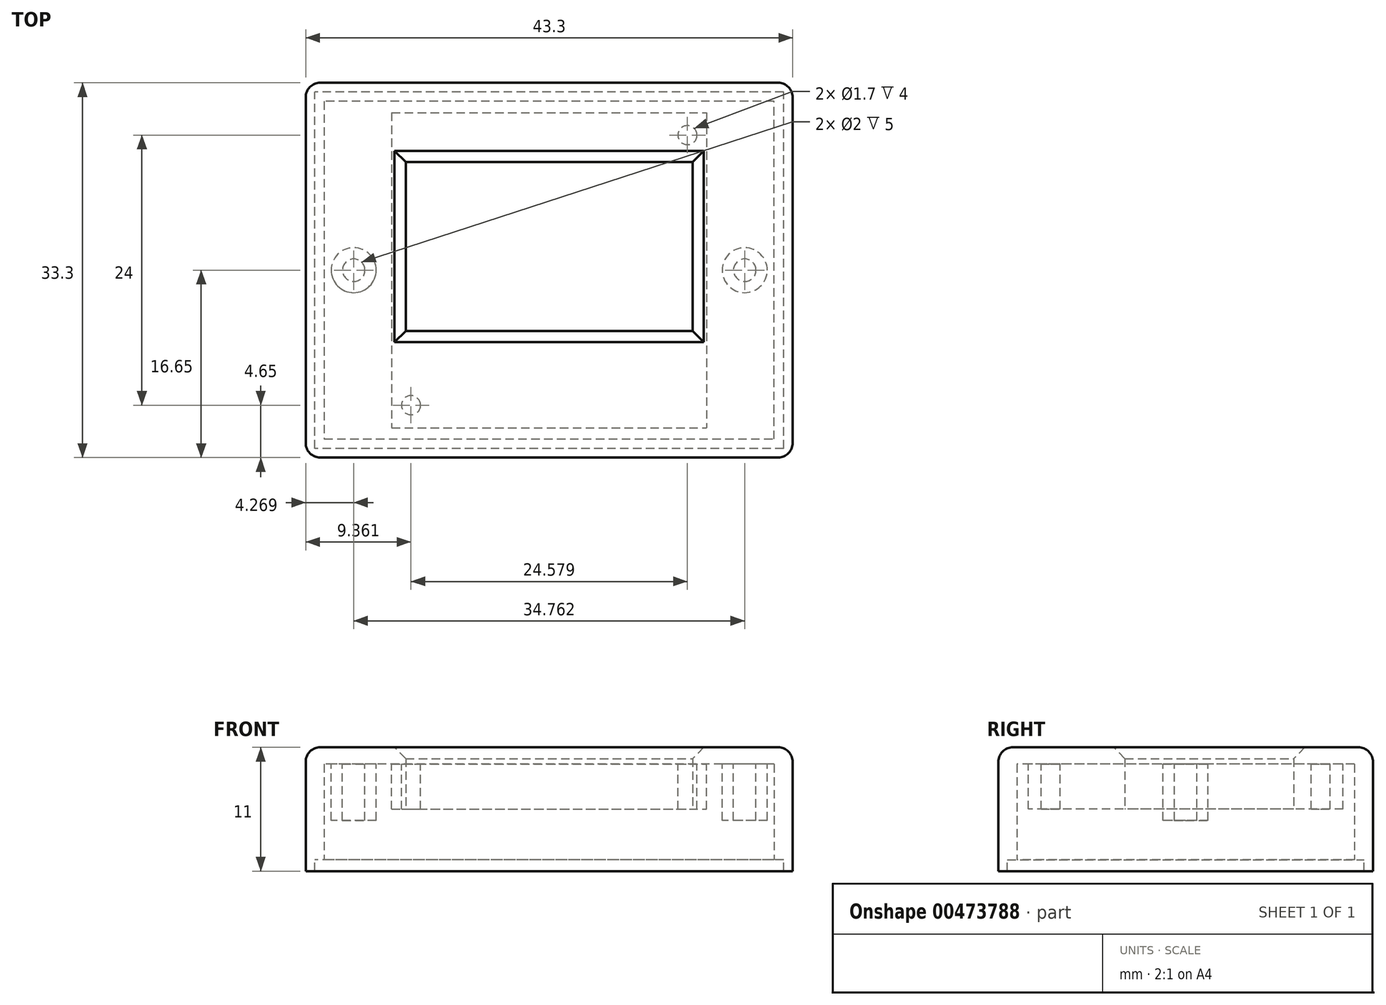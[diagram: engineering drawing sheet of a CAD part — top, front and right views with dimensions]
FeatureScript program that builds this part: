
annotation { "Feature Type Name" : "Feature", "Feature Type Description" : "" }
export const myFeature = defineFeature(function(context is Context, id is Id, definition is map)
    precondition{}
    {
        {
            var Q0;
            Q0=qCreatedBy(makeId("Top.planeOp"),FACE);
            var sketch = newSketch(context, id + "F0", { "sketchPlane" : qUnion([Q0])});
            skPoint(sketch, "E0.middle", {"position": v(0, 0) * mm});
            skLineSegment(sketch, "E1.0", {"start": v(21.65, -16.65) * mm, "end": v(-21.65, -16.65) * mm});
            skLineSegment(sketch, "E1.1", {"start": v(21.65, -16.65) * mm, "end": v(21.65, 16.65) * mm});
            skLineSegment(sketch, "E1.2", {"start": v(21.65, 16.65) * mm, "end": v(-21.65, 16.65) * mm});
            skLineSegment(sketch, "E1.3", {"start": v(-21.65, -16.65) * mm, "end": v(-21.65, 16.65) * mm});
            skSolve(sketch);
        }
        {
            var Q0;
            Q0=qSketchRegion(id+"F0",true);
            extrude(context, id + "F1", {"entities" : qUnion([Q0]), "depth" : 10 * mm});
        }
        {
            var Q0;
            Q0=makeQuery(id+"F0.imprint","IMPRINT",FACE,{"disambiguationData":[TD([[makeQuery(id+"F0.imprint","IMPRINT",EDGE,{"derivedFrom":sQuery(id+"F0.wireOp",EDGE,"E1.0")}),-1.0]])]});
            var sketch = newSketch(context, id + "F2", { "sketchPlane" : qUnion([Q0])});
            skLineSegment(sketch, "E2.0", {"start": v(-20, 15) * mm, "end": v(-20, -15) * mm});
            skLineSegment(sketch, "E2.1", {"start": v(20, 15) * mm, "end": v(-20, 15) * mm});
            skLineSegment(sketch, "E2.2", {"start": v(20, -15) * mm, "end": v(20, 15) * mm});
            skLineSegment(sketch, "E2.3", {"start": v(-20, -15) * mm, "end": v(20, -15) * mm});
            skSolve(sketch);
        }
        {
            var Q0;
            Q0=qSketchRegion(id+"F2",true);
            extrude(context, id + "F3", {"entities" : qUnion([Q0]), "operationType" : NewBodyOperationType.REMOVE, "depth" : 8.5 * mm});
        }
        {
            var Q0;
            Q0=makeQuery(id+"F3.boolean.opBoolean","COPY",FACE,{"derivedFrom":makeQuery(id+"F3.opExtrude","CAP_FACE",FACE,{"disambiguationData":[OSD([sQuery(id+"F2.wireOp",EDGE,"E2.0"),sQuery(id+"F2.wireOp",EDGE,"E2.1"),sQuery(id+"F2.wireOp",EDGE,"E2.2"),sQuery(id+"F2.wireOp",EDGE,"E2.3")])],"isStart":false})});
            var sketch = newSketch(context, id + "F4", { "sketchPlane" : qUnion([Q0])});
            skLineSegment(sketch, "E3.bottom", {"start": v(-21.65, 16.65) * mm, "end": v(21.65, 16.65) * mm});
            skLineSegment(sketch, "E3.top", {"start": v(-21.65, -16.65) * mm, "end": v(21.65, -16.65) * mm});
            skLineSegment(sketch, "E3.left", {"start": v(-21.65, 16.65) * mm, "end": v(-21.65, -16.65) * mm});
            skLineSegment(sketch, "E3.right", {"start": v(21.65, 16.65) * mm, "end": v(21.65, -16.65) * mm});
            skLineSegment(sketch, "E4.bottom", {"start": v(-14, -14) * mm, "end": v(14, -14) * mm});
            skLineSegment(sketch, "E4.top", {"start": v(-14, 14) * mm, "end": v(14, 14) * mm});
            skLineSegment(sketch, "E4.left", {"start": v(-14, -14) * mm, "end": v(-14, 14) * mm});
            skLineSegment(sketch, "E4.right", {"start": v(14, -14) * mm, "end": v(14, 14) * mm});
            skPoint(sketch, "E4.middle", {"position": v(0, 0) * mm});
            skLineSegment(sketch, "E5.bottom", {"start": v(-12.75, -9.6) * mm, "end": v(12.75, -9.6) * mm});
            skLineSegment(sketch, "E5.top", {"start": v(-12.75, 5.4) * mm, "end": v(12.75, 5.4) * mm});
            skLineSegment(sketch, "E5.left", {"start": v(-12.75, -9.6) * mm, "end": v(-12.75, 5.4) * mm});
            skLineSegment(sketch, "E5.right", {"start": v(12.75, -9.6) * mm, "end": v(12.75, 5.4) * mm});
            skPoint(sketch, "E6", {"position": v(0, -9.6) * mm});
            skLineSegment(sketch, "E7", {"start": v(0, -15) * mm, "end": v(0, 15) * mm, "construction": true});
            skCircle(sketch, "E8", {"center": v(-12.29, -12) * mm, "radius": 0.85 * mm});
            skLineSegment(sketch, "E9", {"start": v(-21.65, 0) * mm, "end": v(21.65, 0) * mm, "construction": true});
            skCircle(sketch, "E10.MirrorC", {"center": v(-12.29, 12) * mm, "radius": 0.85 * mm});
            skLineSegment(sketch, "E11.MirrorCS", {"start": v(0, 15) * mm, "end": v(0, -15) * mm, "construction": true});
            skCircle(sketch, "E12.MirrorC", {"center": v(12.29, 12) * mm, "radius": 0.85 * mm});
            skCircle(sketch, "E13.MirrorC", {"center": v(12.29, -12) * mm, "radius": 0.85 * mm});
            skSolve(sketch);
        }
        {
            var Q0;
            Q0=makeQuery(id+"F4.imprint","IMPRINT",FACE,{"disambiguationData":[TD([[makeQuery(id+"F4.imprint","IMPRINT",EDGE,{"derivedFrom":sQuery(id+"F4.wireOp",EDGE,"E5.bottom")}),1.0]])]});
            extrude(context, id + "F5", {"entities" : qUnion([Q0]), "operationType" : NewBodyOperationType.REMOVE, "oppositeDirection" : true, "depth" : 25 * mm});
        }
        {
            var Q0;
            Q0=makeQuery(id+"F4.imprint","IMPRINT",FACE,{"disambiguationData":[TD([[makeQuery(id+"F4.imprint","IMPRINT",EDGE,{"derivedFrom":sQuery(id+"F4.wireOp",EDGE,"E12.MirrorC")}),1.0]])]});
            var Q1;
            Q1=makeQuery(id+"F4.imprint","IMPRINT",FACE,{"disambiguationData":[TD([[makeQuery(id+"F4.imprint","IMPRINT",EDGE,{"derivedFrom":sQuery(id+"F4.wireOp",EDGE,"E10.MirrorC")}),-1.0]])]});
            var Q2;
            Q2=makeQuery(id+"F4.imprint","IMPRINT",FACE,{"disambiguationData":[TD([[makeQuery(id+"F4.imprint","IMPRINT",EDGE,{"derivedFrom":sQuery(id+"F4.wireOp",EDGE,"E8")}),1.0]])]});
            var Q3;
            Q3=makeQuery(id+"F4.imprint","IMPRINT",FACE,{"disambiguationData":[TD([[makeQuery(id+"F4.imprint","IMPRINT",EDGE,{"derivedFrom":sQuery(id+"F4.wireOp",EDGE,"E13.MirrorC")}),-1.0]])]});
            extrude(context, id + "F6", {"entities" : qUnion([Q0, Q1, Q2, Q3]), "operationType" : NewBodyOperationType.ADD, "depth" : 4 * mm});
        }
        {
            var Q0;
            Q0=makeQuery(id+"F1.opExtrude","CAP_FACE",FACE,{"disambiguationData":[OSD([sQuery(id+"F0.wireOp",EDGE,"E1.0"),sQuery(id+"F0.wireOp",EDGE,"E1.1"),sQuery(id+"F0.wireOp",EDGE,"E1.2"),sQuery(id+"F0.wireOp",EDGE,"E1.3")])],"isStart":true});
            var sketch = newSketch(context, id + "F7", { "sketchPlane" : qUnion([Q0])});
            skLineSegment(sketch, "E14.0", {"start": v(20.85, 15.85) * mm, "end": v(-20.85, 15.85) * mm});
            skLineSegment(sketch, "E14.1", {"start": v(20.85, 15.85) * mm, "end": v(20.85, -15.85) * mm});
            skLineSegment(sketch, "E14.2", {"start": v(20.85, -15.85) * mm, "end": v(-20.85, -15.85) * mm});
            skLineSegment(sketch, "E14.3", {"start": v(-20.85, 15.85) * mm, "end": v(-20.85, -15.85) * mm});
            skLineSegment(sketch, "E15.bottom", {"start": v(-21.65, 16.65) * mm, "end": v(21.65, 16.65) * mm});
            skLineSegment(sketch, "E15.top", {"start": v(-21.65, -16.65) * mm, "end": v(21.65, -16.65) * mm});
            skLineSegment(sketch, "E15.left", {"start": v(-21.65, 16.65) * mm, "end": v(-21.65, -16.65) * mm});
            skLineSegment(sketch, "E15.right", {"start": v(21.65, 16.65) * mm, "end": v(21.65, -16.65) * mm});
            skSolve(sketch);
        }
        {
            var Q0;
            Q0=qSketchRegion(id+"F7",true);
            extrude(context, id + "F8", {"entities" : qUnion([Q0]), "operationType" : NewBodyOperationType.ADD, "depth" : 1 * mm});
        }
        {
            var Q0;
            Q0=makeQuery(id+"F4.imprint","IMPRINT",FACE,{"disambiguationData":[TD([[makeQuery(id+"F4.imprint","IMPRINT",EDGE,{"derivedFrom":sQuery(id+"F4.wireOp",EDGE,"E4.bottom")}),-1.0]])]});
            var sketch = newSketch(context, id + "F9", { "sketchPlane" : qUnion([Q0])});
            skCircle(sketch, "E16", {"center": v(-17.38, 0) * mm, "radius": 2 * mm});
            skCircle(sketch, "E17", {"center": v(-17.38, 0) * mm, "radius": 1 * mm});
            skSolve(sketch);
        }
        {
            var Q0;
            Q0=qSketchRegion(id+"F9",true);
            extrude(context, id + "F10", {"entities" : qUnion([Q0]), "depth" : 5 * mm});
        }
        {
            var Q0;
            Q0=makeQuery(id+"F10.opExtrude","SWEPT_BODY",BODY,{"disambiguationData":[OSD([sQuery(id+"F9.wireOp",EDGE,"E16"),sQuery(id+"F9.wireOp",EDGE,"E17")])]});
            var Q1;
            Q1=qCreatedBy(makeId("Right.planeOp"),FACE);
            mirror(context, id + "F11", {"operationType" : NewBodyOperationType.ADD, "entities" : qUnion([Q0]), "mirrorPlane" : qUnion([Q1])});
        }
        {
            var Q0;
            Q0=makeQuery(id+"F5.boolean.opBoolean","INTERSECT",EDGE,{"derivedFrom":[makeQuery(id+"F1.opExtrude","CAP_FACE",FACE,{"disambiguationData":[OSD([sQuery(id+"F0.wireOp",EDGE,"E1.0"),sQuery(id+"F0.wireOp",EDGE,"E1.1"),sQuery(id+"F0.wireOp",EDGE,"E1.2"),sQuery(id+"F0.wireOp",EDGE,"E1.3")])],"isStart":false}),makeQuery(id+"F5.opExtrude","SWEPT_FACE",FACE,{"disambiguationData":[OSD([sQuery(id+"F4.wireOp",EDGE,"E5.bottom")])]})]});
            var Q1;
            Q1=makeQuery(id+"F5.boolean.opBoolean","INTERSECT",EDGE,{"derivedFrom":[makeQuery(id+"F1.opExtrude","CAP_FACE",FACE,{"disambiguationData":[OSD([sQuery(id+"F0.wireOp",EDGE,"E1.0"),sQuery(id+"F0.wireOp",EDGE,"E1.1"),sQuery(id+"F0.wireOp",EDGE,"E1.2"),sQuery(id+"F0.wireOp",EDGE,"E1.3")])],"isStart":false}),makeQuery(id+"F5.opExtrude","SWEPT_FACE",FACE,{"disambiguationData":[OSD([sQuery(id+"F4.wireOp",EDGE,"E5.left")])]})]});
            var Q2;
            Q2=makeQuery(id+"F5.boolean.opBoolean","INTERSECT",EDGE,{"derivedFrom":[makeQuery(id+"F1.opExtrude","CAP_FACE",FACE,{"disambiguationData":[OSD([sQuery(id+"F0.wireOp",EDGE,"E1.0"),sQuery(id+"F0.wireOp",EDGE,"E1.1"),sQuery(id+"F0.wireOp",EDGE,"E1.2"),sQuery(id+"F0.wireOp",EDGE,"E1.3")])],"isStart":false}),makeQuery(id+"F5.opExtrude","SWEPT_FACE",FACE,{"disambiguationData":[OSD([sQuery(id+"F4.wireOp",EDGE,"E5.top")])]})]});
            var Q3;
            Q3=makeQuery(id+"F5.boolean.opBoolean","INTERSECT",EDGE,{"derivedFrom":[makeQuery(id+"F1.opExtrude","CAP_FACE",FACE,{"disambiguationData":[OSD([sQuery(id+"F0.wireOp",EDGE,"E1.0"),sQuery(id+"F0.wireOp",EDGE,"E1.1"),sQuery(id+"F0.wireOp",EDGE,"E1.2"),sQuery(id+"F0.wireOp",EDGE,"E1.3")])],"isStart":false}),makeQuery(id+"F5.opExtrude","SWEPT_FACE",FACE,{"disambiguationData":[OSD([sQuery(id+"F4.wireOp",EDGE,"E5.right")])]})]});
            chamfer(context, id + "F12", {"entities" : qUnion([Q0, Q1, Q2, Q3]), "width" : 1 * mm, "tangentPropagation" : true});
        }
        {
            var Q0;
            Q0=makeQuery(id+"F8.boolean.opBoolean","MERGE",EDGE,{"derivedFrom":[makeQuery(id+"F1.opExtrude","SWEPT_EDGE",EDGE,{"disambiguationData":[OSD([sQuery(id+"F0.wireOp",EDGE,"E1.2"),sQuery(id+"F0.wireOp",EDGE,"E1.3")])]}),makeQuery(id+"F8.opExtrude","SWEPT_EDGE",EDGE,{"disambiguationData":[OSD([sQuery(id+"F7.wireOp",EDGE,"E15.top"),sQuery(id+"F7.wireOp",EDGE,"E15.left")])]})]});
            var Q1;
            Q1=makeQuery(id+"F8.boolean.opBoolean","MERGE",EDGE,{"derivedFrom":[makeQuery(id+"F1.opExtrude","SWEPT_EDGE",EDGE,{"disambiguationData":[OSD([sQuery(id+"F0.wireOp",EDGE,"E1.1"),sQuery(id+"F0.wireOp",EDGE,"E1.2")])]}),makeQuery(id+"F8.opExtrude","SWEPT_EDGE",EDGE,{"disambiguationData":[OSD([sQuery(id+"F7.wireOp",EDGE,"E15.top"),sQuery(id+"F7.wireOp",EDGE,"E15.right")])]})]});
            var Q2;
            Q2=makeQuery(id+"F8.boolean.opBoolean","MERGE",EDGE,{"derivedFrom":[makeQuery(id+"F1.opExtrude","SWEPT_EDGE",EDGE,{"disambiguationData":[OSD([sQuery(id+"F0.wireOp",EDGE,"E1.0"),sQuery(id+"F0.wireOp",EDGE,"E1.1")])]}),makeQuery(id+"F8.opExtrude","SWEPT_EDGE",EDGE,{"disambiguationData":[OSD([sQuery(id+"F7.wireOp",EDGE,"E15.bottom"),sQuery(id+"F7.wireOp",EDGE,"E15.right")])]})]});
            var Q3;
            Q3=makeQuery(id+"F8.boolean.opBoolean","MERGE",EDGE,{"derivedFrom":[makeQuery(id+"F1.opExtrude","SWEPT_EDGE",EDGE,{"disambiguationData":[OSD([sQuery(id+"F0.wireOp",EDGE,"E1.0"),sQuery(id+"F0.wireOp",EDGE,"E1.3")])]}),makeQuery(id+"F8.opExtrude","SWEPT_EDGE",EDGE,{"disambiguationData":[OSD([sQuery(id+"F7.wireOp",EDGE,"E15.bottom"),sQuery(id+"F7.wireOp",EDGE,"E15.left")])]})]});
            var Q4;
            Q4=makeQuery(id+"F1.opExtrude","CAP_EDGE",EDGE,{"disambiguationData":[OSD([sQuery(id+"F0.wireOp",EDGE,"E1.0")])],"isStart":false});
            var Q5;
            Q5=makeQuery(id+"F1.opExtrude","CAP_EDGE",EDGE,{"disambiguationData":[OSD([sQuery(id+"F0.wireOp",EDGE,"E1.3")])],"isStart":false});
            var Q6;
            Q6=makeQuery(id+"F1.opExtrude","CAP_EDGE",EDGE,{"disambiguationData":[OSD([sQuery(id+"F0.wireOp",EDGE,"E1.1")])],"isStart":false});
            var Q7;
            Q7=makeQuery(id+"F1.opExtrude","CAP_EDGE",EDGE,{"disambiguationData":[OSD([sQuery(id+"F0.wireOp",EDGE,"E1.2")])],"isStart":false});
            fillet(context, id + "F13", {"entities" : qUnion([Q0, Q1, Q2, Q3, Q4, Q5, Q6, Q7]), "radius" : 1.3 * mm, "tangentPropagation" : true, "allowEdgeOverflow" : false});
        }
    });
